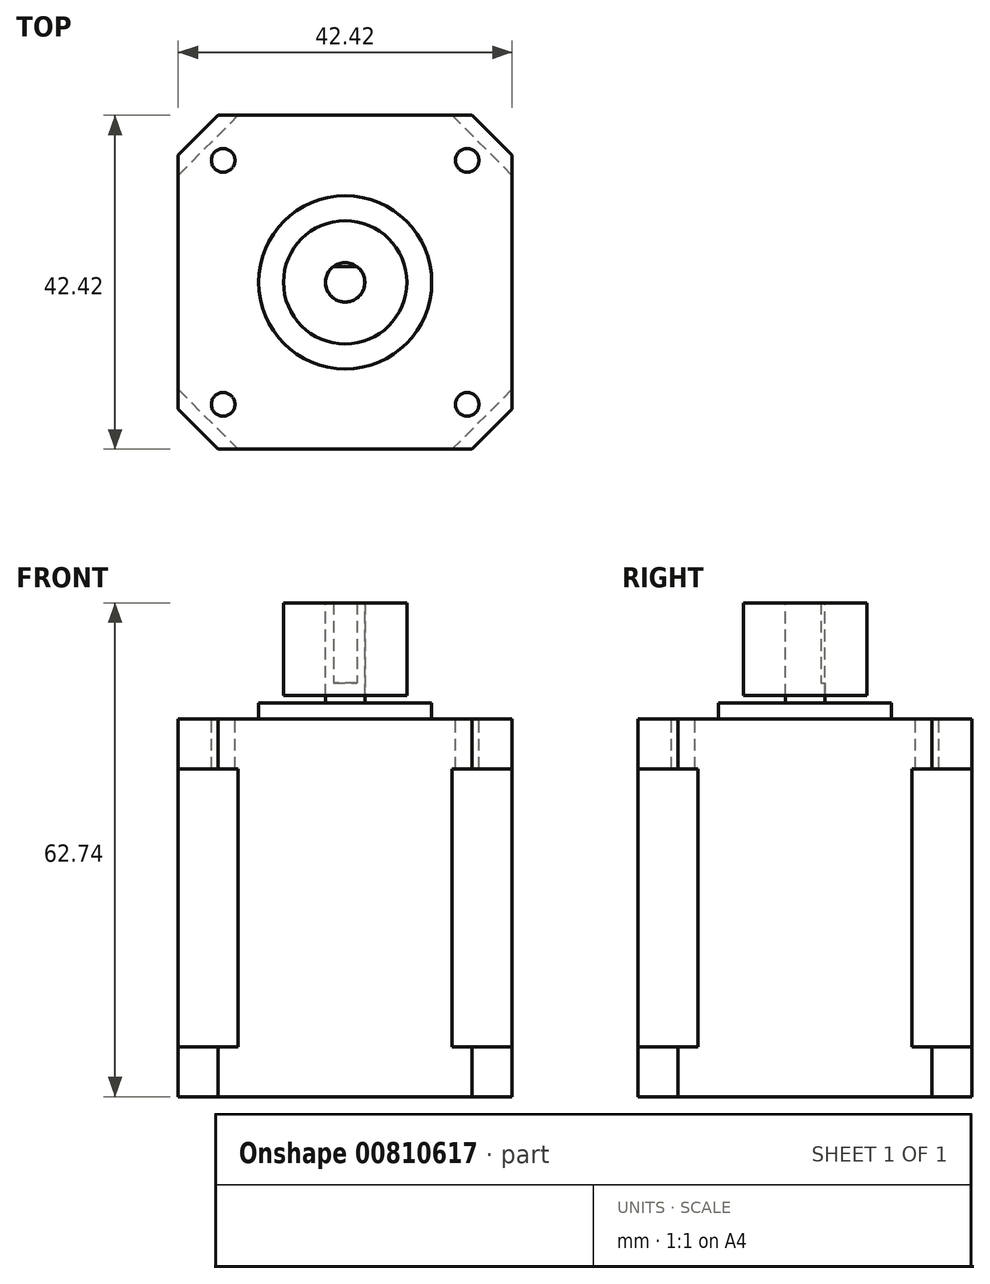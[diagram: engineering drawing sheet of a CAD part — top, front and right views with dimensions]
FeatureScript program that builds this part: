
annotation { "Feature Type Name" : "Feature", "Feature Type Description" : "" }
export const myFeature = defineFeature(function(context is Context, id is Id, definition is map)
    precondition{}
    {
        {
            var Q0;
            Q0=qCreatedBy(makeId("Top.planeOp"),FACE);
            var sketch = newSketch(context, id + "F0", { "sketchPlane" : qUnion([Q0]), "asVersion" : FeatureScriptVersionNumber.V236_DEFAULT_MAX_ASSEMBLIES});
            skLineSegment(sketch, "E0.bottom", {"start": v(-21.2, 21.2) * mm, "end": v(21.2, 21.2) * mm});
            skLineSegment(sketch, "E0.top", {"start": v(-21.2, -21.2) * mm, "end": v(21.2, -21.2) * mm});
            skLineSegment(sketch, "E0.left", {"start": v(-21.2, 21.2) * mm, "end": v(-21.2, -21.2) * mm});
            skLineSegment(sketch, "E0.right", {"start": v(21.2, 21.2) * mm, "end": v(21.2, -21.2) * mm});
            skSolve(sketch);
        }
        {
            var Q0;
            Q0=makeQuery(id+"F0.imprint","IMPRINT",FACE,{"disambiguationData":[TD([[makeQuery(id+"F0.imprint","IMPRINT",EDGE,{"derivedFrom":sQuery(id+"F0.wireOp",EDGE,"E0.bottom")}),-1.0]])]});
            extrude(context, id + "F1", {"entities" : qUnion([Q0]), "depth" : 35.3 * mm, "symmetric" : true});
        }
        {
            var Q0;
            Q0=makeQuery(id+"F1.opExtrude","SWEPT_EDGE",EDGE,{"disambiguationData":[OSD([sQuery(id+"F0.wireOp",EDGE,"E0.bottom"),sQuery(id+"F0.wireOp",EDGE,"E0.right")])]});
            var Q1;
            Q1=makeQuery(id+"F1.opExtrude","SWEPT_EDGE",EDGE,{"disambiguationData":[OSD([sQuery(id+"F0.wireOp",EDGE,"E0.bottom"),sQuery(id+"F0.wireOp",EDGE,"E0.left")])]});
            var Q2;
            Q2=makeQuery(id+"F1.opExtrude","SWEPT_EDGE",EDGE,{"disambiguationData":[OSD([sQuery(id+"F0.wireOp",EDGE,"E0.top"),sQuery(id+"F0.wireOp",EDGE,"E0.left")])]});
            var Q3;
            Q3=makeQuery(id+"F1.opExtrude","SWEPT_EDGE",EDGE,{"disambiguationData":[OSD([sQuery(id+"F0.wireOp",EDGE,"E0.top"),sQuery(id+"F0.wireOp",EDGE,"E0.right")])]});
            chamfer(context, id + "F2", {"entities" : qUnion([Q0, Q1, Q2, Q3]), "width" : 7.62 * mm, "tangentPropagation" : true});
        }
        {
            var Q0;
            Q0=makeQuery(id+"F1.opExtrude","CAP_FACE",FACE,{"disambiguationData":[OSD([sQuery(id+"F0.wireOp",EDGE,"E0.bottom"),sQuery(id+"F0.wireOp",EDGE,"E0.top"),sQuery(id+"F0.wireOp",EDGE,"E0.left"),sQuery(id+"F0.wireOp",EDGE,"E0.right")])],"isStart":false});
            var sketch = newSketch(context, id + "F3", { "sketchPlane" : qUnion([Q0]), "asVersion" : FeatureScriptVersionNumber.V236_DEFAULT_MAX_ASSEMBLIES});
            skLineSegment(sketch, "E1.bottom", {"start": v(-21.2, 21.2) * mm, "end": v(21.2, 21.2) * mm});
            skLineSegment(sketch, "E1.top", {"start": v(-21.2, -21.2) * mm, "end": v(21.2, -21.2) * mm});
            skLineSegment(sketch, "E1.left", {"start": v(-21.2, 21.2) * mm, "end": v(-21.2, -21.2) * mm});
            skLineSegment(sketch, "E1.right", {"start": v(21.2, 21.2) * mm, "end": v(21.2, -21.2) * mm});
            skSolve(sketch);
        }
        {
            var Q0;
            {var subQ0=sQuery(id+"F0.wireOp",EDGE,"E0.top");var subQ1=sQuery(id+"F0.wireOp",EDGE,"E0.right");var subQ2=sQuery(id+"F0.wireOp",EDGE,"E0.bottom");var subQ3=sQuery(id+"F0.wireOp",EDGE,"E0.left");var subQ4=makeQuery(id+"F1.opExtrude","CAP_FACE",FACE,{"disambiguationData":[OSD([subQ2,subQ0,subQ3,subQ1])],"isStart":false});var subQ8=makeQuery(id+"F2.opChamfer","BLEND_EDGE",EDGE,{"blendedFrom":[makeQuery(id+"F1.opExtrude","SWEPT_EDGE",EDGE,{"disambiguationData":[OSD([subQ2,subQ3])]}),subQ4],"blendedInto":[subQ4]});Q0=makeQuery(id+"F3.imprint","IMPRINT",FACE,{"disambiguationData":[TD([[makeQuery(id+"F3.imprint","IMPRINT",EDGE,{"derivedFrom":subQ8}),1.0]])]});}
            var Q1;
            {var subQ0=sQuery(id+"F0.wireOp",EDGE,"E0.bottom");var subQ1=sQuery(id+"F0.wireOp",EDGE,"E0.right");var subQ2=makeQuery(id+"F2.opChamfer","BLEND_EDGE",EDGE,{"blendedFrom":[makeQuery(id+"F1.opExtrude","SWEPT_EDGE",EDGE,{"disambiguationData":[OSD([subQ0,subQ1])]}),makeQuery(id+"F1.opExtrude","CAP_FACE",FACE,{"disambiguationData":[OSD([subQ0,sQuery(id+"F0.wireOp",EDGE,"E0.top"),sQuery(id+"F0.wireOp",EDGE,"E0.left"),subQ1])],"isStart":false})],"blendedInto":[makeQuery(id+"F1.opExtrude","CAP_FACE",FACE,{"disambiguationData":[OSD([subQ0,sQuery(id+"F0.wireOp",EDGE,"E0.top"),sQuery(id+"F0.wireOp",EDGE,"E0.left"),subQ1])],"isStart":false})]});Q1=makeQuery(id+"F3.imprint","IMPRINT",FACE,{"disambiguationData":[TD([[makeQuery(id+"F3.imprint","IMPRINT",EDGE,{"derivedFrom":subQ2}),-1.0]])]});}
            var Q2;
            {var subQ0=sQuery(id+"F0.wireOp",EDGE,"E0.bottom");var subQ1=sQuery(id+"F0.wireOp",EDGE,"E0.left");var subQ2=makeQuery(id+"F2.opChamfer","BLEND_EDGE",EDGE,{"blendedFrom":[makeQuery(id+"F1.opExtrude","SWEPT_EDGE",EDGE,{"disambiguationData":[OSD([subQ0,subQ1])]}),makeQuery(id+"F1.opExtrude","CAP_FACE",FACE,{"disambiguationData":[OSD([subQ0,sQuery(id+"F0.wireOp",EDGE,"E0.top"),subQ1,sQuery(id+"F0.wireOp",EDGE,"E0.right")])],"isStart":false})],"blendedInto":[makeQuery(id+"F1.opExtrude","CAP_FACE",FACE,{"disambiguationData":[OSD([subQ0,sQuery(id+"F0.wireOp",EDGE,"E0.top"),subQ1,sQuery(id+"F0.wireOp",EDGE,"E0.right")])],"isStart":false})]});Q2=makeQuery(id+"F3.imprint","IMPRINT",FACE,{"disambiguationData":[TD([[makeQuery(id+"F3.imprint","IMPRINT",EDGE,{"derivedFrom":subQ2}),-1.0]])]});}
            var Q3;
            {var subQ0=sQuery(id+"F0.wireOp",EDGE,"E0.top");var subQ1=sQuery(id+"F0.wireOp",EDGE,"E0.left");var subQ2=makeQuery(id+"F2.opChamfer","BLEND_EDGE",EDGE,{"blendedFrom":[makeQuery(id+"F1.opExtrude","SWEPT_EDGE",EDGE,{"disambiguationData":[OSD([subQ0,subQ1])]}),makeQuery(id+"F1.opExtrude","CAP_FACE",FACE,{"disambiguationData":[OSD([sQuery(id+"F0.wireOp",EDGE,"E0.bottom"),subQ0,subQ1,sQuery(id+"F0.wireOp",EDGE,"E0.right")])],"isStart":false})],"blendedInto":[makeQuery(id+"F1.opExtrude","CAP_FACE",FACE,{"disambiguationData":[OSD([sQuery(id+"F0.wireOp",EDGE,"E0.bottom"),subQ0,subQ1,sQuery(id+"F0.wireOp",EDGE,"E0.right")])],"isStart":false})]});Q3=makeQuery(id+"F3.imprint","IMPRINT",FACE,{"disambiguationData":[TD([[makeQuery(id+"F3.imprint","IMPRINT",EDGE,{"derivedFrom":subQ2}),-1.0]])]});}
            var Q4;
            {var subQ0=sQuery(id+"F0.wireOp",EDGE,"E0.top");var subQ1=sQuery(id+"F0.wireOp",EDGE,"E0.right");var subQ2=makeQuery(id+"F2.opChamfer","BLEND_EDGE",EDGE,{"blendedFrom":[makeQuery(id+"F1.opExtrude","SWEPT_EDGE",EDGE,{"disambiguationData":[OSD([subQ0,subQ1])]}),makeQuery(id+"F1.opExtrude","CAP_FACE",FACE,{"disambiguationData":[OSD([sQuery(id+"F0.wireOp",EDGE,"E0.bottom"),subQ0,sQuery(id+"F0.wireOp",EDGE,"E0.left"),subQ1])],"isStart":false})],"blendedInto":[makeQuery(id+"F1.opExtrude","CAP_FACE",FACE,{"disambiguationData":[OSD([sQuery(id+"F0.wireOp",EDGE,"E0.bottom"),subQ0,sQuery(id+"F0.wireOp",EDGE,"E0.left"),subQ1])],"isStart":false})]});Q4=makeQuery(id+"F3.imprint","IMPRINT",FACE,{"disambiguationData":[TD([[makeQuery(id+"F3.imprint","IMPRINT",EDGE,{"derivedFrom":subQ2}),-1.0]])]});}
            extrude(context, id + "F4", {"entities" : qUnion([Q0, Q1, Q2, Q3, Q4]), "operationType" : NewBodyOperationType.ADD, "depth" : 6.35 * mm});
        }
        {
            var Q0;
            Q0=makeQuery(id+"F4.opExtrude","SWEPT_EDGE",EDGE,{"disambiguationData":[OSD([sQuery(id+"F3.wireOp",EDGE,"E1.bottom"),sQuery(id+"F3.wireOp",EDGE,"E1.right")])]});
            var Q1;
            Q1=makeQuery(id+"F4.opExtrude","SWEPT_EDGE",EDGE,{"disambiguationData":[OSD([sQuery(id+"F3.wireOp",EDGE,"E1.bottom"),sQuery(id+"F3.wireOp",EDGE,"E1.left")])]});
            var Q2;
            Q2=makeQuery(id+"F4.opExtrude","SWEPT_EDGE",EDGE,{"disambiguationData":[OSD([sQuery(id+"F3.wireOp",EDGE,"E1.top"),sQuery(id+"F3.wireOp",EDGE,"E1.left")])]});
            var Q3;
            Q3=makeQuery(id+"F4.opExtrude","SWEPT_EDGE",EDGE,{"disambiguationData":[OSD([sQuery(id+"F3.wireOp",EDGE,"E1.top"),sQuery(id+"F3.wireOp",EDGE,"E1.right")])]});
            chamfer(context, id + "F5", {"entities" : qUnion([Q0, Q1, Q2, Q3]), "width" : 5.08 * mm, "tangentPropagation" : true});
        }
        {
            var Q0;
            Q0=makeQuery(id+"F1.opExtrude","CAP_FACE",FACE,{"disambiguationData":[OSD([sQuery(id+"F0.wireOp",EDGE,"E0.bottom"),sQuery(id+"F0.wireOp",EDGE,"E0.top"),sQuery(id+"F0.wireOp",EDGE,"E0.left"),sQuery(id+"F0.wireOp",EDGE,"E0.right")])],"isStart":true});
            var sketch = newSketch(context, id + "F6", { "sketchPlane" : qUnion([Q0]), "asVersion" : FeatureScriptVersionNumber.V236_DEFAULT_MAX_ASSEMBLIES});
            skLineSegment(sketch, "E2.0.0", {"start": v(-16.13, 21.2) * mm, "end": v(16.13, 21.2) * mm});
            skLineSegment(sketch, "E2.0.1", {"start": v(16.13, 21.2) * mm, "end": v(21.2, 16.13) * mm});
            skLineSegment(sketch, "E2.0.2", {"start": v(21.2, -16.13) * mm, "end": v(21.2, 16.13) * mm});
            skLineSegment(sketch, "E2.0.3", {"start": v(21.2, -16.13) * mm, "end": v(16.13, -21.2) * mm});
            skLineSegment(sketch, "E2.0.4", {"start": v(-16.13, -21.2) * mm, "end": v(16.13, -21.2) * mm});
            skLineSegment(sketch, "E2.0.5", {"start": v(-16.13, -21.2) * mm, "end": v(-21.2, -16.13) * mm});
            skLineSegment(sketch, "E2.0.6", {"start": v(-21.2, -16.13) * mm, "end": v(-21.2, 16.13) * mm});
            skLineSegment(sketch, "E2.0.7", {"start": v(-21.2, 16.13) * mm, "end": v(-16.13, 21.2) * mm});
            skSolve(sketch);
        }
        {
            var Q0;
            {var subQ3=sQuery(id+"F6.wireOp",EDGE,"E2.0.7");Q0=makeQuery(id+"F6.imprint","IMPRINT",FACE,{"disambiguationData":[TD([[makeQuery(id+"F6.imprint","IMPRINT",EDGE,{"derivedFrom":subQ3}),-1.0]])]});}
            var Q1;
            {var subQ4=sQuery(id+"F6.wireOp",EDGE,"E2.0.1");Q1=makeQuery(id+"F6.imprint","IMPRINT",FACE,{"disambiguationData":[TD([[makeQuery(id+"F6.imprint","IMPRINT",EDGE,{"derivedFrom":subQ4}),-1.0]])]});}
            var Q2;
            {var subQ4=sQuery(id+"F6.wireOp",EDGE,"E2.0.3");Q2=makeQuery(id+"F6.imprint","IMPRINT",FACE,{"disambiguationData":[TD([[makeQuery(id+"F6.imprint","IMPRINT",EDGE,{"derivedFrom":subQ4}),-1.0]])]});}
            var Q3;
            {var subQ4=sQuery(id+"F6.wireOp",EDGE,"E2.0.5");Q3=makeQuery(id+"F6.imprint","IMPRINT",FACE,{"disambiguationData":[TD([[makeQuery(id+"F6.imprint","IMPRINT",EDGE,{"derivedFrom":subQ4}),-1.0]])]});}
            var Q4;
            {var subQ0=sQuery(id+"F0.wireOp",EDGE,"E0.top");var subQ1=sQuery(id+"F0.wireOp",EDGE,"E0.right");var subQ2=sQuery(id+"F0.wireOp",EDGE,"E0.bottom");var subQ3=sQuery(id+"F0.wireOp",EDGE,"E0.left");var subQ4=makeQuery(id+"F1.opExtrude","CAP_FACE",FACE,{"disambiguationData":[OSD([subQ2,subQ0,subQ3,subQ1])],"isStart":true});var subQ8=makeQuery(id+"F2.opChamfer","BLEND_EDGE",EDGE,{"blendedFrom":[makeQuery(id+"F1.opExtrude","SWEPT_EDGE",EDGE,{"disambiguationData":[OSD([subQ2,subQ3])]}),subQ4],"blendedInto":[subQ4]});Q4=makeQuery(id+"F6.imprint","IMPRINT",FACE,{"disambiguationData":[TD([[makeQuery(id+"F6.imprint","IMPRINT",EDGE,{"derivedFrom":subQ8}),1.0]])]});}
            extrude(context, id + "F7", {"entities" : qUnion([Q0, Q1, Q2, Q3, Q4]), "operationType" : NewBodyOperationType.ADD, "depth" : 6.35 * mm});
        }
        {
            var Q0;
            Q0=makeQuery(id+"F4.opExtrude","CAP_FACE",FACE,{"disambiguationData":[OSD([sQuery(id+"F3.wireOp",EDGE,"E1.bottom"),sQuery(id+"F3.wireOp",EDGE,"E1.top"),sQuery(id+"F3.wireOp",EDGE,"E1.left"),sQuery(id+"F3.wireOp",EDGE,"E1.right")])],"isStart":false});
            var sketch = newSketch(context, id + "F8", { "sketchPlane" : qUnion([Q0]), "asVersion" : FeatureScriptVersionNumber.V236_DEFAULT_MAX_ASSEMBLIES});
            skCircle(sketch, "E3", {"center": v(0, 0) * mm, "radius": 11 * mm});
            skSolve(sketch);
        }
        {
            var Q0;
            Q0=makeQuery(id+"F8.imprint","IMPRINT",FACE,{"disambiguationData":[TD([[makeQuery(id+"F8.imprint","IMPRINT",EDGE,{"derivedFrom":sQuery(id+"F8.wireOp",EDGE,"E3")}),1.0]])]});
            extrude(context, id + "F9", {"entities" : qUnion([Q0]), "operationType" : NewBodyOperationType.ADD, "depth" : 2.03 * mm});
        }
        {
            var Q0;
            Q0=makeQuery(id+"F9.opExtrude","CAP_FACE",FACE,{"disambiguationData":[OSD([sQuery(id+"F8.wireOp",EDGE,"E3")])],"isStart":false});
            var sketch = newSketch(context, id + "F10", { "sketchPlane" : qUnion([Q0]), "asVersion" : FeatureScriptVersionNumber.V236_DEFAULT_MAX_ASSEMBLIES});
            skCircle(sketch, "E4", {"center": v(0, 0) * mm, "radius": 2.5 * mm});
            skSolve(sketch);
        }
        {
            var Q0;
            Q0=makeQuery(id+"F10.imprint","IMPRINT",FACE,{"disambiguationData":[TD([[makeQuery(id+"F10.imprint","IMPRINT",EDGE,{"derivedFrom":sQuery(id+"F10.wireOp",EDGE,"E4")}),1.0]])]});
            extrude(context, id + "F11", {"entities" : qUnion([Q0]), "operationType" : NewBodyOperationType.ADD, "depth" : 12.7 * mm});
        }
        {
            var Q0;
            Q0=makeQuery(id+"F11.opExtrude","CAP_FACE",FACE,{"disambiguationData":[OSD([sQuery(id+"F10.wireOp",EDGE,"E4")])],"isStart":false});
            var sketch = newSketch(context, id + "F12", { "sketchPlane" : qUnion([Q0]), "asVersion" : FeatureScriptVersionNumber.V236_DEFAULT_MAX_ASSEMBLIES});
            skLineSegment(sketch, "E5.bottom", {"start": v(-2.63, 2.93) * mm, "end": v(2.62, 2.93) * mm});
            skLineSegment(sketch, "E5.top", {"start": v(-2.63, 2) * mm, "end": v(2.62, 2) * mm});
            skLineSegment(sketch, "E5.left", {"start": v(-2.63, 2.93) * mm, "end": v(-2.63, 2) * mm});
            skLineSegment(sketch, "E5.right", {"start": v(2.62, 2.93) * mm, "end": v(2.62, 2) * mm});
            skSolve(sketch);
        }
        {
            var Q0;
            {var subQ0=makeQuery(id+"F11.opExtrude","CAP_EDGE",EDGE,{"disambiguationData":[OSD([sQuery(id+"F10.wireOp",EDGE,"E4")])],"isStart":false});var subQ1=sQuery(id+"F12.wireOp",EDGE,"E5.top");var subQ3=makeQuery(id+"F12.imprint","INTERSECT",VERTEX,{"disambiguationData":[OD(0.0)],"derivedFrom":[subQ0,subQ1]});Q0=qUnion([makeQuery(id+"F12.imprint","IMPRINT",FACE,{"disambiguationData":[TD([[makeQuery(id+"F12.imprint","IMPRINT",EDGE,{"derivedFrom":sQuery(id+"F12.wireOp",EDGE,"E5.bottom")}),-1.0]])]}),makeQuery(id+"F12.imprint","IMPRINT",FACE,{"disambiguationData":[TD([[makeQuery(id+"F12.imprint","IMPRINT",EDGE,{"disambiguationData":[TD([[subQ3,-1.0]])],"derivedFrom":subQ1}),1.0]])]})]);}
            extrude(context, id + "F13", {"entities" : qUnion([Q0]), "operationType" : NewBodyOperationType.REMOVE, "oppositeDirection" : true, "depth" : 10.16 * mm});
        }
        {
            var Q0;
            Q0=makeQuery(id+"F4.opExtrude","CAP_FACE",FACE,{"disambiguationData":[OSD([sQuery(id+"F3.wireOp",EDGE,"E1.bottom"),sQuery(id+"F3.wireOp",EDGE,"E1.top"),sQuery(id+"F3.wireOp",EDGE,"E1.left"),sQuery(id+"F3.wireOp",EDGE,"E1.right")])],"isStart":false});
            var sketch = newSketch(context, id + "F14", { "sketchPlane" : qUnion([Q0]), "asVersion" : FeatureScriptVersionNumber.V236_DEFAULT_MAX_ASSEMBLIES});
            skLineSegment(sketch, "E6.rect.bottom", {"start": v(15.5, 15.5) * mm, "end": v(-15.5, 15.5) * mm, "construction": true});
            skLineSegment(sketch, "E6.rect.top", {"start": v(15.5, -15.5) * mm, "end": v(-15.5, -15.5) * mm, "construction": true});
            skLineSegment(sketch, "E6.rect.left", {"start": v(15.5, 15.5) * mm, "end": v(15.5, -15.5) * mm, "construction": true});
            skLineSegment(sketch, "E6.rect.right", {"start": v(-15.5, 15.5) * mm, "end": v(-15.5, -15.5) * mm, "construction": true});
            skPoint(sketch, "E6.rect.middle", {"position": v(0, 0) * mm});
            skCircle(sketch, "E7", {"center": v(-15.5, 15.5) * mm, "radius": 1.5 * mm});
            skCircle(sketch, "E8", {"center": v(15.5, 15.5) * mm, "radius": 1.5 * mm});
            skCircle(sketch, "E9", {"center": v(15.5, -15.5) * mm, "radius": 1.5 * mm});
            skCircle(sketch, "E10", {"center": v(-15.5, -15.5) * mm, "radius": 1.5 * mm});
            skSolve(sketch);
        }
        {
            var Q0;
            Q0=makeQuery(id+"F14.imprint","IMPRINT",FACE,{"disambiguationData":[TD([[makeQuery(id+"F14.imprint","IMPRINT",EDGE,{"derivedFrom":sQuery(id+"F14.wireOp",EDGE,"E7")}),1.0]])]});
            var Q1;
            Q1=makeQuery(id+"F14.imprint","IMPRINT",FACE,{"disambiguationData":[TD([[makeQuery(id+"F14.imprint","IMPRINT",EDGE,{"derivedFrom":sQuery(id+"F14.wireOp",EDGE,"E8")}),1.0]])]});
            var Q2;
            Q2=makeQuery(id+"F14.imprint","IMPRINT",FACE,{"disambiguationData":[TD([[makeQuery(id+"F14.imprint","IMPRINT",EDGE,{"derivedFrom":sQuery(id+"F14.wireOp",EDGE,"E9")}),1.0]])]});
            var Q3;
            Q3=makeQuery(id+"F14.imprint","IMPRINT",FACE,{"disambiguationData":[TD([[makeQuery(id+"F14.imprint","IMPRINT",EDGE,{"derivedFrom":sQuery(id+"F14.wireOp",EDGE,"E10")}),1.0]])]});
            extrude(context, id + "F15", {"entities" : qUnion([Q0, Q1, Q2, Q3]), "operationType" : NewBodyOperationType.REMOVE, "oppositeDirection" : true, "depth" : 6.35 * mm});
        }
        {
            var Q0;
            Q0=makeQuery(id+"F11.opExtrude","CAP_FACE",FACE,{"disambiguationData":[OSD([sQuery(id+"F10.wireOp",EDGE,"E4")])],"isStart":false});
            var sketch = newSketch(context, id + "F16", { "sketchPlane" : qUnion([Q0]), "asVersion" : FeatureScriptVersionNumber.V236_DEFAULT_MAX_ASSEMBLIES});
            skCircle(sketch, "E11", {"center": v(0, 0) * mm, "radius": 7.83 * mm});
            skCircle(sketch, "E12", {"center": v(0, 0) * mm, "radius": 2.5 * mm});
            skSolve(sketch);
        }
        {
            var Q0;
            Q0=makeQuery(id+"F16.imprint","IMPRINT",FACE,{"disambiguationData":[TD([[makeQuery(id+"F16.imprint","IMPRINT",EDGE,{"derivedFrom":sQuery(id+"F16.wireOp",EDGE,"E11")}),1.0]])]});
            extrude(context, id + "F17", {"entities" : qUnion([Q0]), "oppositeDirection" : true, "depth" : 11.8 * mm});
        }
    });
